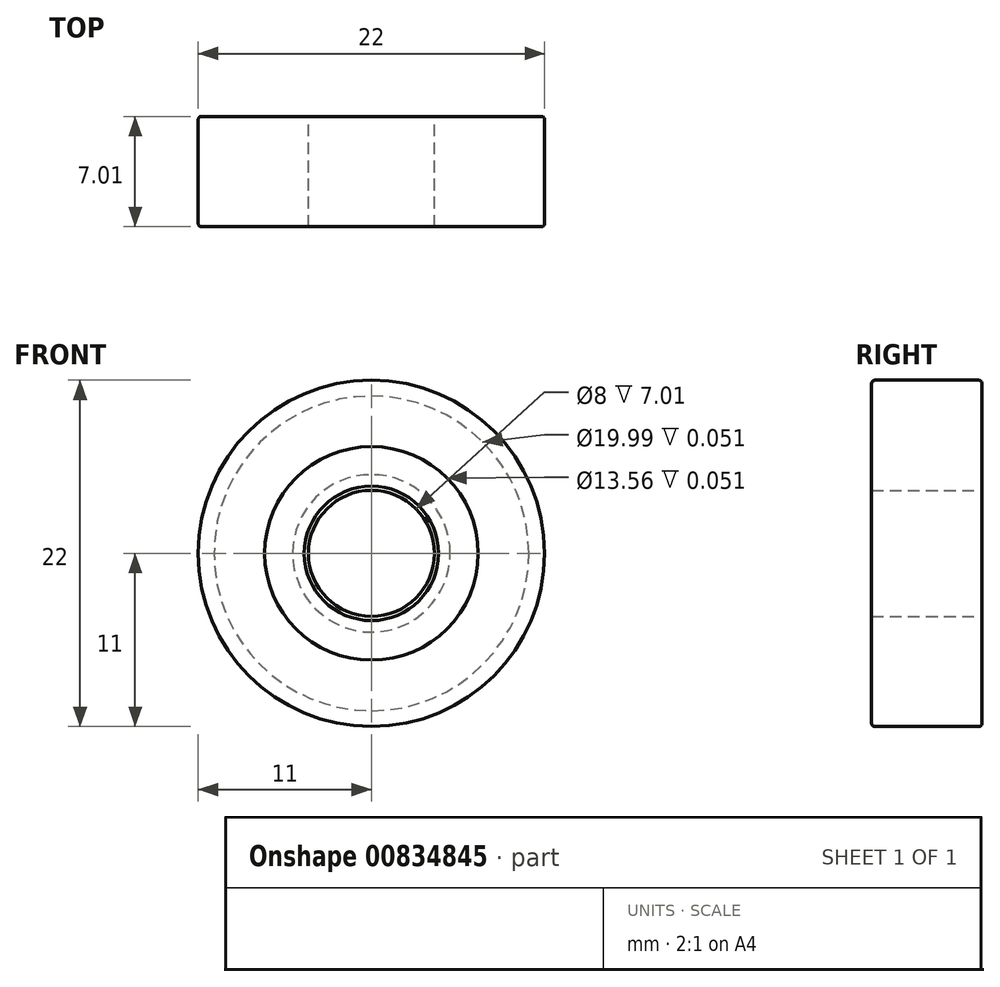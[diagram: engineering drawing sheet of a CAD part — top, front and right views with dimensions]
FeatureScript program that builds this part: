
annotation { "Feature Type Name" : "Feature", "Feature Type Description" : "" }
export const myFeature = defineFeature(function(context is Context, id is Id, definition is map)
    precondition{}
    {
        {
            var Q0;
            Q0=qCreatedBy(makeId("Front.planeOp"),FACE);
            var sketch = newSketch(context, id + "F0", { "sketchPlane" : qUnion([Q0])});
            skCircle(sketch, "E0", {"center": v(0, 0) * mm, "radius": 11 * mm});
            skCircle(sketch, "E1", {"center": v(0, 0) * mm, "radius": 4 * mm});
            skSolve(sketch);
        }
        {
            var Q0;
            Q0=qCreatedBy(makeId("Front.planeOp"),FACE);
            var sketch = newSketch(context, id + "F1", { "sketchPlane" : qUnion([Q0])});
            skCircle(sketch, "E2", {"center": v(0, 0) * mm, "radius": 5 * mm});
            skCircle(sketch, "E3", {"center": v(0, 0) * mm, "radius": 10 * mm});
            skSolve(sketch);
        }
        {
            var Q0;
            Q0=qSketchRegion(id+"F0",true);
            extrude(context, id + "F2", {"entities" : qUnion([Q0]), "offsetDistance" : 25.4 * mm, "depth" : 7 * mm});
        }
        {
            var Q0;
            Q0=makeQuery(id+"F1.imprint","IMPRINT",FACE,{"disambiguationData":[TD([[makeQuery(id+"F1.imprint","IMPRINT",EDGE,{"derivedFrom":sQuery(id+"F1.wireOp",EDGE,"E2")}),-1.0]])]});
            var Q1;
            Q1=makeQuery(id+"F2.opExtrude","CAP_FACE",FACE,{"disambiguationData":[OSD([sQuery(id+"F0.wireOp",EDGE,"E0"),sQuery(id+"F0.wireOp",EDGE,"E1")])],"isStart":false});
            extrude(context, id + "F3", {"entities" : qUnion([Q0, Q1]), "operationType" : NewBodyOperationType.REMOVE, "depth" : 0.05 * mm});
        }
        {
            var Q0;
            Q0=makeQuery(id+"F2.opExtrude","CAP_FACE",FACE,{"disambiguationData":[OSD([sQuery(id+"F0.wireOp",EDGE,"E0"),sQuery(id+"F0.wireOp",EDGE,"E1")])],"isStart":false});
            var sketch = newSketch(context, id + "F4", { "sketchPlane" : qUnion([Q0])});
            skCircle(sketch, "E4", {"center": v(0, 0) * mm, "radius": 4.27 * mm});
            skCircle(sketch, "E5", {"center": v(0, 0) * mm, "radius": 6.78 * mm});
            skSolve(sketch);
        }
        {
            var Q0;
            Q0=makeQuery(id+"F4.imprint","IMPRINT",FACE,{"disambiguationData":[TD([[makeQuery(id+"F4.imprint","IMPRINT",EDGE,{"derivedFrom":sQuery(id+"F4.wireOp",EDGE,"E4")}),-1.0]])]});
            extrude(context, id + "F5", {"entities" : qUnion([Q0]), "operationType" : NewBodyOperationType.REMOVE, "oppositeDirection" : true, "depth" : 0.05 * mm});
        }
        {
            var Q0;
            Q0=makeQuery(id+"F2.opExtrude","CAP_EDGE",EDGE,{"disambiguationData":[OSD([sQuery(id+"F0.wireOp",EDGE,"E0")])],"isStart":false});
            var Q1;
            Q1=makeQuery(id+"F2.opExtrude","CAP_EDGE",EDGE,{"disambiguationData":[OSD([sQuery(id+"F0.wireOp",EDGE,"E0")])],"isStart":true});
            fillet(context, id + "F6", {"entities" : qUnion([Q0, Q1]), "radius" : 0.2 * mm, "tangentPropagation" : true, "allowEdgeOverflow" : false});
        }
    });
